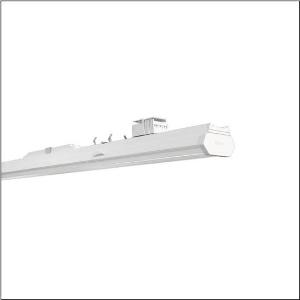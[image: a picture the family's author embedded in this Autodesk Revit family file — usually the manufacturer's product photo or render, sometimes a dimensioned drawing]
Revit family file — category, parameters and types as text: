
# Revit family: licross_r__11_protected_mo_51tp11cn49xg_312d
name_source: partatom
category: Lighting Fixtures
units: mm (PartAtom-declared; Revit-internal decimal feet)

## family parameters
Cut with Voids When Loaded = No
Host = Face
Light Source = No
Part Type = Normal
Room Calculation Point = No
Round Connector Dimension = Use Diameter
Shared = No

## types (1)
- --- (1 x LED, 9030 lm, 49.4 W, 4000K)
    Apparent Load = 49 VA
    CIE Flux Codes = 83 94 98 100 100
    Color Rendering = 80
    Color Temperature = 4000K
    Default Elevation = 1800 mm
    Description = Licross® 11 Protected MO, luminaire insert, of sheet steel, galvanised, coil coated, white, length: 1.500mm, width: 90mm, height: 101mm, LED rated luminous flux: 9.030lm, light colour: 840, control gear: ON/OFF Multilumen, CLOi, with plug, 3-pole, with phase selection, mains connection: 220..240V, AC, 50/60Hz, start of lifetime: 49W, end of service life: 55W, halogen-free wiring, primary light control with lens, of plastic, primary optical cover: cover, of PMMA, light emission: direct distribution, primary light characteristic: symmetric, protection rating (complete): IP64, insulation class (complete): insulation class I (protective earthing), certification: CE, ENEC, VDE, UKCA, protection symbol: D if used in an environment with conductive dust loads with corresponding accessories, impact resistance: IK06, permissible ambient temperature for indoor applications: -35..+40°C, corresponds to IFS (International Featured Standards) requirements for safety and quality in the food industry, reducing of maximum allowable ambient temperature of 5°C with ceiling mounting, LABS conformity tested according to VDMA 24364:2018-05, packaging unit: 1 piece
    Height = 92 mm
    Lamp = 1 x LED
    Lamp Light Flux = 9030 lm
    Lamp Power = 49.4 W
    Lamp count = 1
    Length = 1500 mm
    Luminous efficacy = 183 lm/W
    Manufacturer = Siteco
    ModVariant = No
    Model = 51TP11CN49XG
    Mounting Place = Ceiling
    Mounting Type = Pendant
    Number of Poles = 1
    OnlyDefault = Yes
    Power Factor = 1
    Product Name = Licross® 11 Protected MO
    Product group = luminaire insert
    ProductGroupID = 901
    Protection Class = Protection class I
    Protection Degree = IP 64
    RLX_Detail_Level = 1
    RLX_Emergency_Light_Flux = 0 lm
    RLX_Emergency_Type = 0
    RLX_Emergency_Type_DB = No
    RlxData = <blob elided: 21829 chars, md5=58adb9a7>
    Socket = socket
    Standby Power = 0 W
    System Light Flux = 9030 lm
    System Power = 49 W
    Type Comments = factory setting: luminous flux: 100 % | (A | C | E) | 113 mA
    Type Image = l_1256148.jpg
    URL = http://relux.com
    VarID = @adj_055103
    Voltage = 0 V
    Weight = 0.00 kg
    Width = 88 mm

## geometry (parser evidence)
native form markers: Blend x4, Sweep x10
no freeform markers — native parametric forms only
